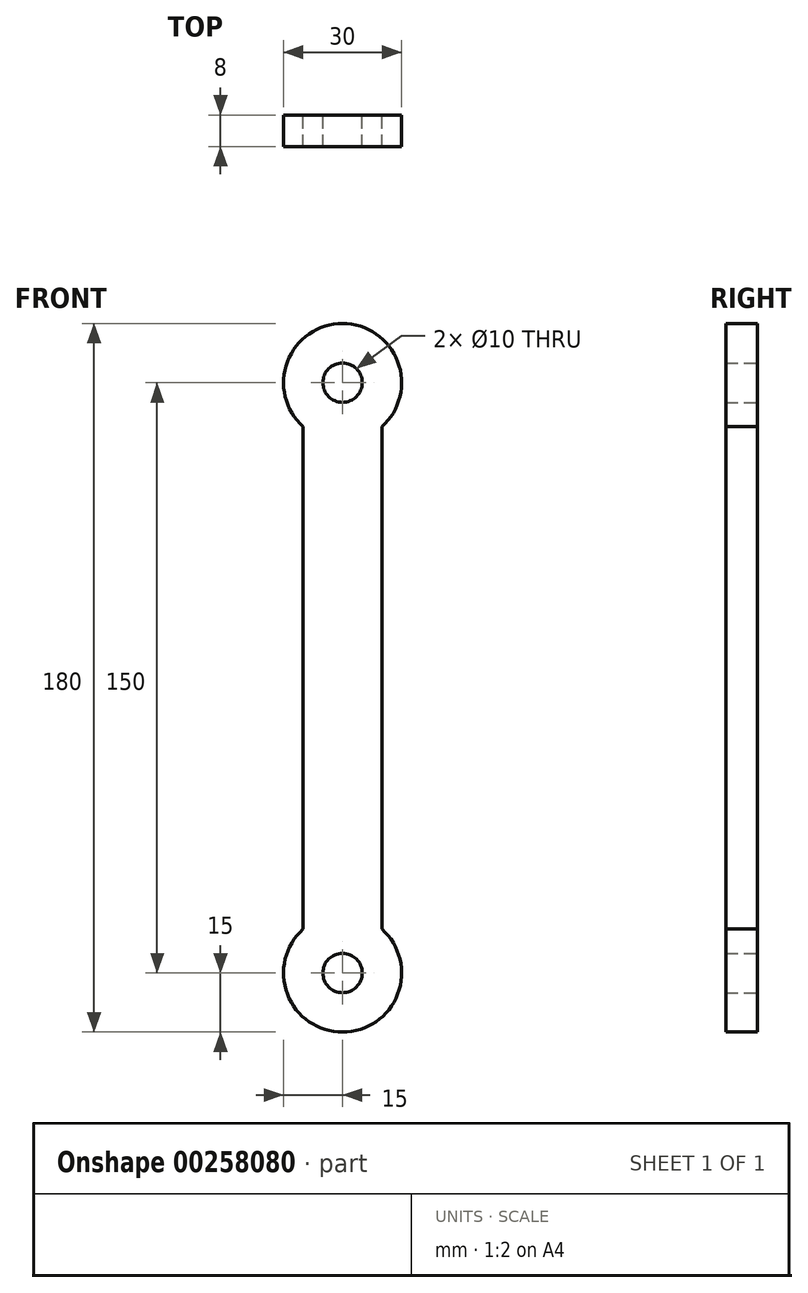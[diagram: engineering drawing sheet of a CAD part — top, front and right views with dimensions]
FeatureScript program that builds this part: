
annotation { "Feature Type Name" : "Feature", "Feature Type Description" : "" }
export const myFeature = defineFeature(function(context is Context, id is Id, definition is map)
    precondition{}
    {
        {
            var Q0;
            Q0=qCreatedBy(makeId("Front.planeOp"),FACE);
            var sketch = newSketch(context, id + "F0", { "sketchPlane" : qUnion([Q0])});
            skCircle(sketch, "E0", {"center": v(0, 0) * mm, "radius": 15 * mm});
            skCircle(sketch, "E1", {"center": v(0, -150) * mm, "radius": 15 * mm});
            skLineSegment(sketch, "E2", {"start": v(0, 0) * mm, "end": v(0, -150) * mm});
            skLineSegment(sketch, "E3.0", {"start": v(-10, 11.18) * mm, "end": v(-10, -138.82) * mm});
            skLineSegment(sketch, "E4.0", {"start": v(10, -11.18) * mm, "end": v(10, -138.82) * mm});
            skCircle(sketch, "E5", {"center": v(0, 0) * mm, "radius": 5 * mm});
            skCircle(sketch, "E6", {"center": v(0, -150) * mm, "radius": 5 * mm});
            skSolve(sketch);
        }
        {
            var Q0;
            Q0 = qSketchRegion(id + "F0", true);
            extrude(context, id + "F1", {"entities" : qUnion([Q0]), "depth" : 8 * mm, "symmetric" : true});
        }
    });
